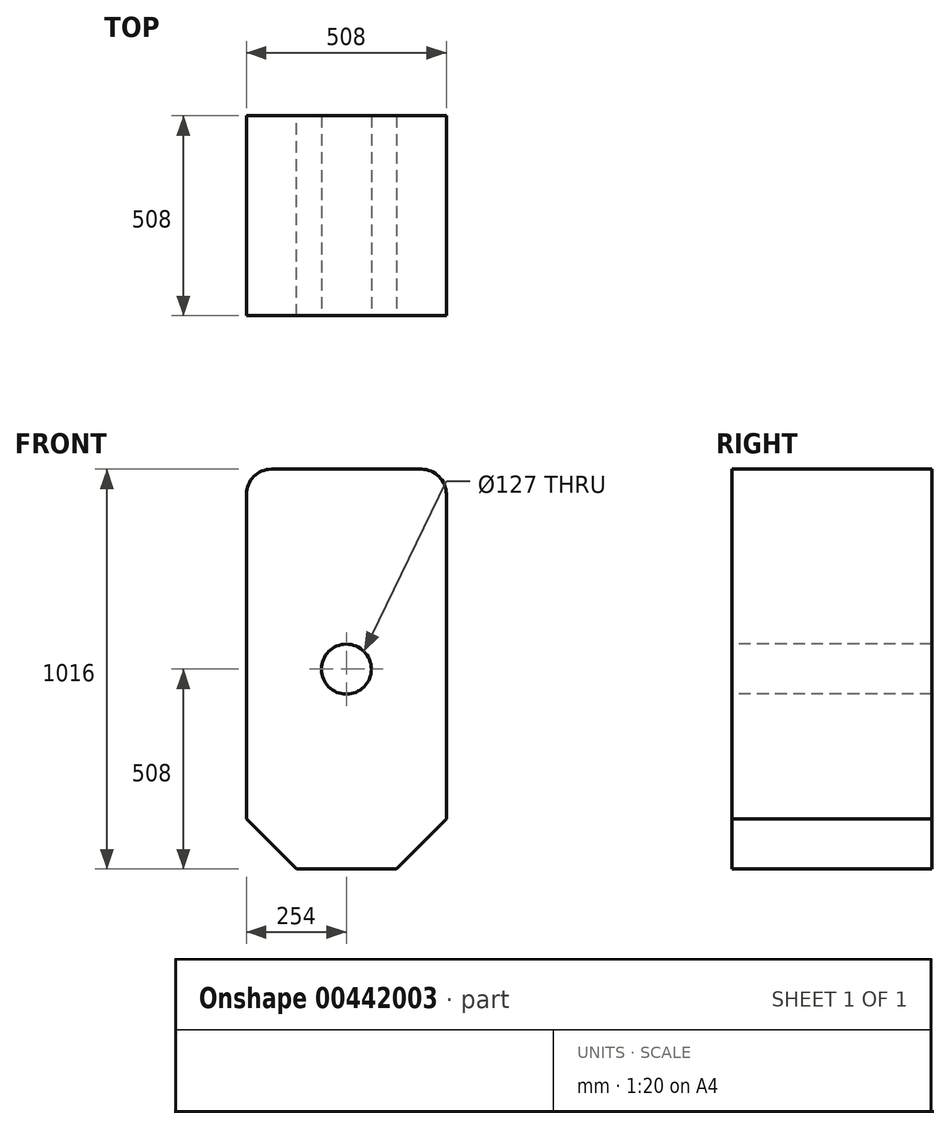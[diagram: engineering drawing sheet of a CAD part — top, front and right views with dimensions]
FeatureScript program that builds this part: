
annotation { "Feature Type Name" : "Feature", "Feature Type Description" : "" }
export const myFeature = defineFeature(function(context is Context, id is Id, definition is map)
    precondition{}
    {
        {
            var Q0;
            Q0=qCreatedBy(makeId("Front.planeOp"),FACE);
            var sketch = newSketch(context, id + "F0", { "sketchPlane" : qUnion([Q0])});
            skLineSegment(sketch, "E0.bottom", {"start": v(-254, 508) * mm, "end": v(254, 508) * mm});
            skLineSegment(sketch, "E0.top", {"start": v(-254, -508) * mm, "end": v(254, -508) * mm});
            skLineSegment(sketch, "E0.left", {"start": v(-254, 508) * mm, "end": v(-254, -508) * mm});
            skLineSegment(sketch, "E0.right", {"start": v(254, 508) * mm, "end": v(254, -508) * mm});
            skPoint(sketch, "E0.middle", {"position": v(0, 0) * mm});
            skSolve(sketch);
        }
        {
            var Q0;
            Q0=makeQuery(id+"F0.imprint","IMPRINT",FACE,{"disambiguationData":[TD([[makeQuery(id+"F0.imprint","IMPRINT",EDGE,{"derivedFrom":sQuery(id+"F0.wireOp",EDGE,"E0.bottom")}),-1.0]])]});
            extrude(context, id + "F1", {"entities" : qUnion([Q0]), "depth" : 508 * mm});
        }
        {
            var Q0;
            Q0=makeQuery(id+"F1.opExtrude","CAP_FACE",FACE,{"disambiguationData":[OSD([sQuery(id+"F0.wireOp",EDGE,"E0.bottom"),sQuery(id+"F0.wireOp",EDGE,"E0.top"),sQuery(id+"F0.wireOp",EDGE,"E0.left"),sQuery(id+"F0.wireOp",EDGE,"E0.right")])],"isStart":false});
            var sketch = newSketch(context, id + "F2", { "sketchPlane" : qUnion([Q0])});
            skCircle(sketch, "E1", {"center": v(0, 0) * mm, "radius": 63.5 * mm});
            skSolve(sketch);
        }
        {
            var Q0;
            Q0=makeQuery(id+"F2.imprint","IMPRINT",FACE,{"disambiguationData":[TD([[makeQuery(id+"F2.imprint","IMPRINT",EDGE,{"derivedFrom":sQuery(id+"F2.wireOp",EDGE,"E1")}),1.0]])]});
            extrude(context, id + "F3", {"entities" : qUnion([Q0]), "operationType" : NewBodyOperationType.REMOVE, "endBound" : BoundingType.THROUGH_ALL, "oppositeDirection" : true, "depth" : 25.4 * mm});
        }
        {
            var Q0;
            Q0=makeQuery(id+"F1.opExtrude","SWEPT_EDGE",EDGE,{"disambiguationData":[OSD([sQuery(id+"F0.wireOp",EDGE,"E0.bottom"),sQuery(id+"F0.wireOp",EDGE,"E0.right")])]});
            var Q1;
            Q1=makeQuery(id+"F1.opExtrude","SWEPT_EDGE",EDGE,{"disambiguationData":[OSD([sQuery(id+"F0.wireOp",EDGE,"E0.bottom"),sQuery(id+"F0.wireOp",EDGE,"E0.left")])]});
            fillet(context, id + "F4", {"entities" : qUnion([Q0, Q1]), "radius" : 63.5 * mm, "tangentPropagation" : true, "allowEdgeOverflow" : false});
        }
        {
            var Q0;
            Q0=makeQuery(id+"F1.opExtrude","SWEPT_EDGE",EDGE,{"disambiguationData":[OSD([sQuery(id+"F0.wireOp",EDGE,"E0.top"),sQuery(id+"F0.wireOp",EDGE,"E0.right")])]});
            var Q1;
            Q1=makeQuery(id+"F1.opExtrude","SWEPT_EDGE",EDGE,{"disambiguationData":[OSD([sQuery(id+"F0.wireOp",EDGE,"E0.top"),sQuery(id+"F0.wireOp",EDGE,"E0.left")])]});
            chamfer(context, id + "F5", {"entities" : qUnion([Q0, Q1]), "width" : 127 * mm, "tangentPropagation" : true});
        }
    });
